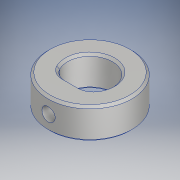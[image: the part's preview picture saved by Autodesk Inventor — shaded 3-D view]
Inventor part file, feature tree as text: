
AUTODESK INVENTOR PART (.ipt)
format: ipt  version: 2019 (Build 230136000, 136)  size: 141,824 bytes
history: native  units: mm
features: hole x2, other x2, fillet x1, chamfer x1
ambient origin geometry x8: Origin, YZ Plane, XZ Plane, XY Plane, X Axis, Y Axis, Z Axis, Center Point
bodies: Solid1 (feature_tree), Body (feature_tree)
feature tree (6):
  hole  "Hole Work Plane"  [1 undecoded]
  hole  "Cable Hole"  [1 undecoded]
  fillet  "Internal Fillet"  Radius=4.05mm
  chamfer  "Safety Chamfer"  Distance=7.0mm
  other  "Body Cross Section"
  other  "Cable Hole Position"
note: 2 required parameter values undecoded (feature->parameter linkage not recoverable at this tier; creation-order binding heuristic only, values carry confidence <= 0.55)
